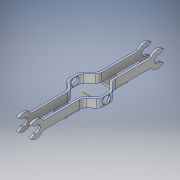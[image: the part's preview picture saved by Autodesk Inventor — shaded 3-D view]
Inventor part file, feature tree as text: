
AUTODESK INVENTOR PART (.ipt)
format: ipt  version: 2018 (Build 220112000, 112)  size: 282,624 bytes
history: native  units: in
note: dims shown in document units (in); Inventor stores cm internally (conversion verified against a paired STEP export)
features: extrude x7, sketch x7, fillet x2, mirror x2, plane x1
ambient origin geometry x8: Origin, YZ Plane, XZ Plane, XY Plane, X Axis, Y Axis, Z Axis, Center Point
bodies: Solid1 (feature_tree)
feature tree (19):
  extrude  "Extrusion1"  Depth=0.12in
  extrude  "Extrusion3"  Depth=0.025in TaperAngle=0.0deg
  fillet  "Fillet4"  Radius=0.025in
  extrude  "Extrusion6"  Depth=0.1in
  extrude  "Extrusion8"  Depth=0.06in TaperAngle=0.0deg
  fillet  "Fillet6"  Radius=0.06in
  extrude  "Extrusion10"  Depth=0.14in TaperAngle=0.0deg
  extrude  "Extrusion11"  Depth=0.174in
  plane  "Work Plane3"
  mirror  "Mirror2"
  mirror  "Mirror3"
  extrude  "Extrusion12"  Depth=0.9963in
  sketch  "Sketch1"  dims[d14=0.08in d15=0.0in d33=0.12in]
  sketch  "Sketch3"  dims[d34=0.12in d35=0.025in d36=0.0in d37=0.025in]
  sketch  "Sketch6"  dims[d45=1.0in d46=0.0in d50=0.1in]
  sketch  "Sketch9"  dims[d51=0.3in d52=1.0in d53=0.0in d65=0.06in]
  sketch  "Sketch11"  dims[d66=0.157in d69=0.14in d70=0.0in]
  sketch  "Sketch12"  dims[d71=0.14in d72=0.0in d73=0.174in]
  sketch  "Sketch13"  dims[d74=0.074in d75=0.9963in d76=0.9963in d77=0.075in d78=1.0in d79=0.0in]
